# Revit family: A7104
name_source: partatom
category: Lighting Fixtures
revit_build: Autodesk Revit Architecture 2012 (Build: 20110309_2315(x64)
units: mm (PartAtom-declared; Revit-internal decimal feet)

## types (2) — shared parameters
Aperture = 1 3/4"
Apparent Load = 0 VA
Default Elevation = 48"
Depth = 6 3/4"
Description = Directional/Accent Pinhole
Finish = Matte Black
Lamp = LED Lamp
Length = 16 3/8"
Manufacturer = Kurt Versen Lighting
Manufacturer Fax = (201)-664-4801
Model = A1704
Product Documentation Link = http://www.kurtversen.com
Product Page URL = http://www.kurtversen.com
URL = http://www.kurtversen.com
Voltage = 277 V
ceiling thickness = -1 1/2"

## per-type parameters (varying)
| type | Ceiling Cut Out | Cone Finish | Inputs Watts | Photometry | Width |
| A1704-14 3/4" Width | 1 3/4" | A7104 Cone : Graphite Cone | 17 W | Web A7104 : A7104_17W_Xicato_1000_lm_3000K | 14 3/4" |
| A1704-16" Width | 4 3/8" | A7104 Cone : Bronze Cone | 38 W | Web A7104 : A7104_38W_Xicato_2000_lm_3000K | 16" |

## geometry (parser evidence)
native form markers: Blend x9, Sweep x8
no freeform markers — native parametric forms only
